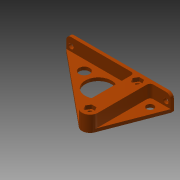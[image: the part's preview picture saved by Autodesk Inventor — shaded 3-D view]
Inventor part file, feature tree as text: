
AUTODESK INVENTOR PART (.ipt)
format: ipt  version: 2013 (Build 170138000, 138)  size: 210,944 bytes
history: native  units: mm
features: extrude x8, sketch x8, fillet x2, projected_geometry x1
ambient origin geometry x8: Origin, YZ Plane, XZ Plane, XY Plane, X Axis, Y Axis, Z Axis, Center Point
bodies: Solid1 (feature_tree)
feature tree (19):
  extrude  "Extrusion1"  Depth=75.0mm
  extrude  "Extrusion2"  Depth=165.0mm
  extrude  "Extrusion3"  Depth=5.0mm
  fillet  "Fillet1"  Radius=45.0mm
  extrude  "Extrusion4"  Depth=20.0mm TaperAngle=0.0deg
  extrude  "Extrusion7"  Depth=150.0mm
  extrude  "Extrusion8"  Depth=12.5mm
  extrude  "Extrusion9"  Depth=5.0mm
  extrude  "Extrusion10"  Depth=6.0mm TaperAngle=0.0deg
  fillet  "Fillet2"  Radius=7.5mm
  sketch  "Sketch1"  dims[d0=12.5mm d1=75.0mm]
  sketch  "Sketch2"  dims[d2=8.1mm d3=165.0mm]
  sketch  "Sketch3"  dims[d4=12.5mm d5=5.0mm d6=45.0mm]
  projected_geometry  "Projected Loop1"
  sketch  "Sketch4"  dims[d7=5.0mm d8=0.0mm d9=20.0mm d10=0.0mm]
  sketch  "Sketch7"  dims[d11=8.1mm d13=150.0mm]
  sketch  "Sketch8"  dims[d14=7.5mm d15=12.5mm]
  sketch  "Sketch9"  dims[d16=20.0mm d17=0.0mm d18=5.0mm]
  sketch  "Sketch10"  dims[d19=13.1mm d20=6.0mm d21=0.0mm d31=7.5mm d33=10.0mm d34=0.0mm d37=7.5mm d39=10.0mm d40=0.0mm d41=7.5mm d43=10.0mm d44=0.0mm d45=7.5mm d47=10.0mm d48=0.0mm d49=7.5mm]
